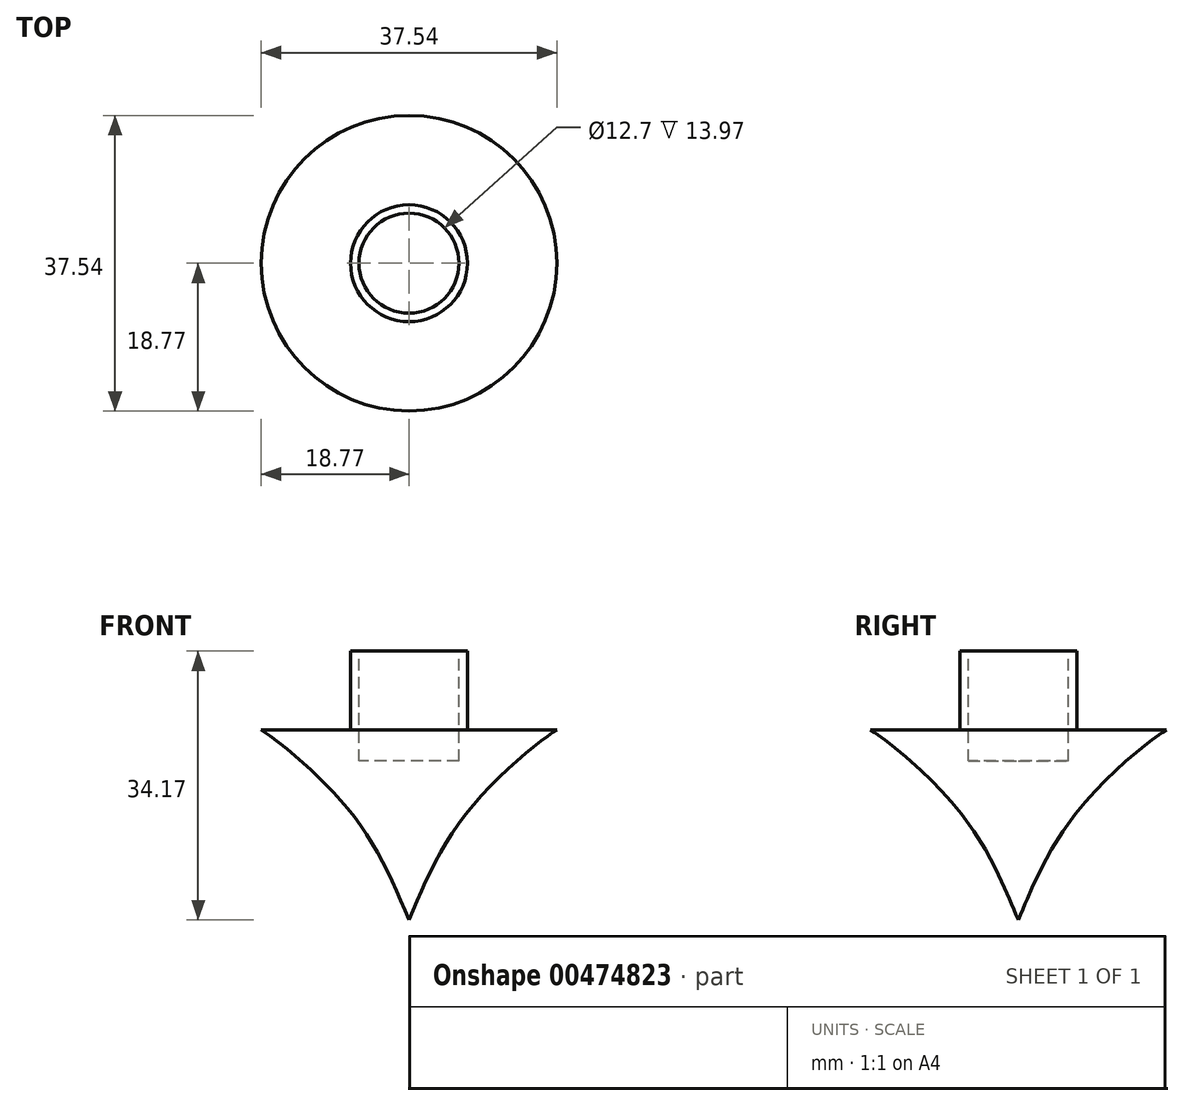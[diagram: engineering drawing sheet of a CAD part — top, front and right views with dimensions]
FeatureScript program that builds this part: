
annotation { "Feature Type Name" : "Feature", "Feature Type Description" : "" }
export const myFeature = defineFeature(function(context is Context, id is Id, definition is map)
    precondition{}
    {
        {
            var Q0;
            Q0=qCreatedBy(makeId("Front.planeOp"),FACE);
            var sketch = newSketch(context, id + "F0", { "sketchPlane" : qUnion([Q0])});
            skFitSpline(sketch, "E0", {"points": [v(0, 0) * mm, v(8.08, 14.52) * mm, v(18.77, 24.12) * mm, v(19.43, 24.34) * mm], "startDerivative": vector(13.05, 31.22) * mm, "endDerivative": vector(4.92, 0.53) * mm});
            skLineSegment(sketch, "E1", {"start": v(18.77, 24.12) * mm, "end": v(7.42, 24.12) * mm});
            skLineSegment(sketch, "E2", {"start": v(7.42, 24.12) * mm, "end": v(7.42, 34.17) * mm});
            skLineSegment(sketch, "E3", {"start": v(7.42, 34.17) * mm, "end": v(0, 34.17) * mm});
            skLineSegment(sketch, "E4", {"start": v(0, 34.17) * mm, "end": v(0, 0) * mm});
            skSolve(sketch);
        }
        {
            var Q0;
            {var subQ0=sQuery(id+"F0.wireOp",EDGE,"E1");Q0=makeQuery(id+"F0.imprint","IMPRINT",FACE,{"disambiguationData":[TD([[makeQuery(id+"F0.imprint","IMPRINT",EDGE,{"derivedFrom":subQ0}),1.0]])]});}
            var Q1;
            Q1=sQuery(id+"F0.wireOp",EDGE,"E4");
            revolve(context, id + "F1", {"entities" : qUnion([Q0]), "axis" : qUnion([Q1]), "revolveType" : RevolveType.FULL});
        }
        {
            var Q0;
            Q0=makeQuery(id+"F1.opRevolve","SWEPT_FACE",FACE,{"disambiguationData":[OSD([sQuery(id+"F0.wireOp",EDGE,"E3")])]});
            var sketch = newSketch(context, id + "F2", { "sketchPlane" : qUnion([Q0])});
            skCircle(sketch, "E5", {"center": v(0, 0) * mm, "radius": 6.35 * mm});
            skSolve(sketch);
        }
        {
            var Q0;
            Q0=makeQuery(id+"F2.imprint","IMPRINT",FACE,{"disambiguationData":[TD([[makeQuery(id+"F2.imprint","IMPRINT",EDGE,{"derivedFrom":sQuery(id+"F2.wireOp",EDGE,"E5")}),1.0]])]});
            extrude(context, id + "F3", {"entities" : qUnion([Q0]), "operationType" : NewBodyOperationType.REMOVE, "oppositeDirection" : true, "depth" : 13.97 * mm});
        }
    });
